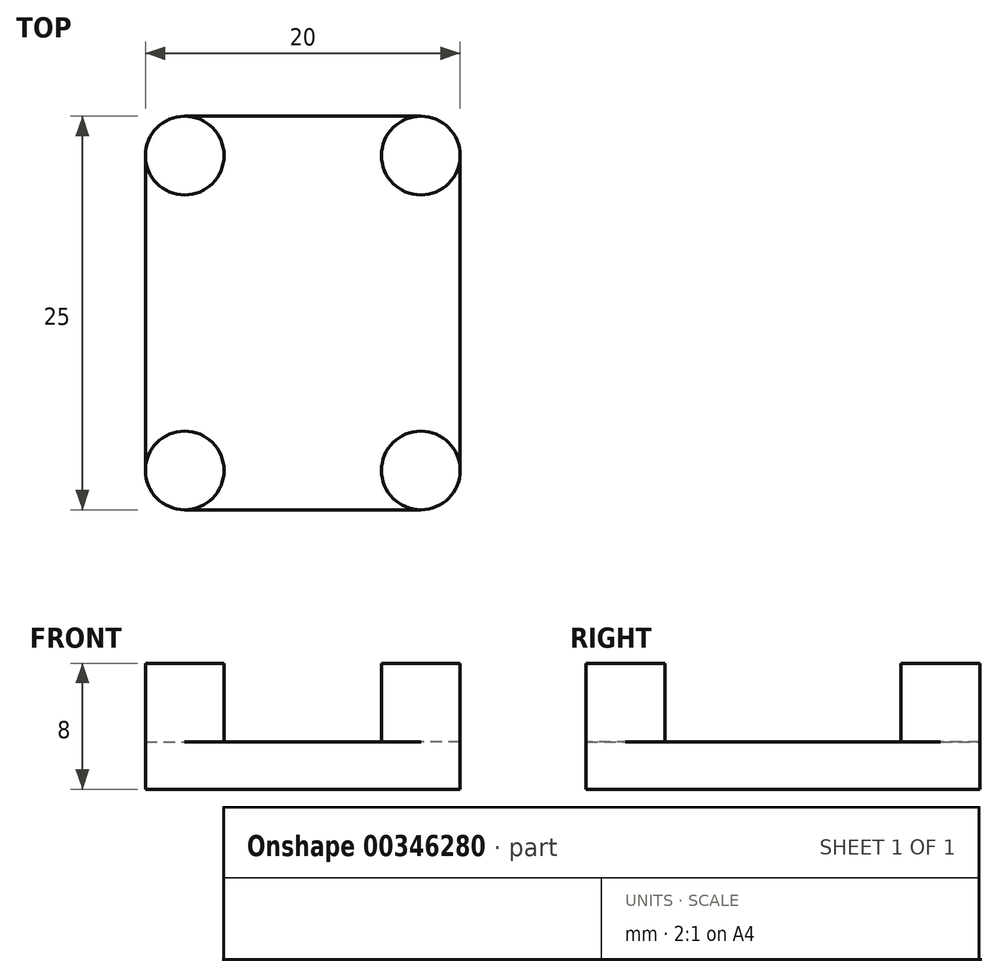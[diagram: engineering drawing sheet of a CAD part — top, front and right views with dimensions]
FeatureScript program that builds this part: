
annotation { "Feature Type Name" : "Feature", "Feature Type Description" : "" }
export const myFeature = defineFeature(function(context is Context, id is Id, definition is map)
    precondition{}
    {
        {
            var Q0;
            Q0=qCreatedBy(makeId("Top.planeOp"),FACE);
            var sketch = newSketch(context, id + "F0", { "sketchPlane" : qUnion([Q0])});
            skLineSegment(sketch, "E0.bottom", {"start": v(7.5, 10) * mm, "end": v(-7.5, 10) * mm, "construction": true});
            skLineSegment(sketch, "E0.top", {"start": v(7.5, -10) * mm, "end": v(-7.5, -10) * mm, "construction": true});
            skLineSegment(sketch, "E0.left", {"start": v(7.5, 10) * mm, "end": v(7.5, -10) * mm, "construction": true});
            skLineSegment(sketch, "E0.right", {"start": v(-7.5, 10) * mm, "end": v(-7.5, -10) * mm, "construction": true});
            skPoint(sketch, "E0.middle", {"position": v(0, 0) * mm});
            skCircle(sketch, "E1", {"center": v(-7.5, 10) * mm, "radius": 2.5 * mm});
            skCircle(sketch, "E2", {"center": v(7.5, 10) * mm, "radius": 2.5 * mm});
            skCircle(sketch, "E3", {"center": v(7.5, -10) * mm, "radius": 2.5 * mm});
            skCircle(sketch, "E4", {"center": v(-7.5, -10) * mm, "radius": 2.5 * mm});
            skLineSegment(sketch, "E5", {"start": v(-10, 10) * mm, "end": v(-10, -10) * mm});
            skLineSegment(sketch, "E6", {"start": v(-7.5, -12.5) * mm, "end": v(7.5, -12.5) * mm});
            skLineSegment(sketch, "E7", {"start": v(10, -10) * mm, "end": v(10, 10) * mm});
            skLineSegment(sketch, "E8", {"start": v(7.5, 12.5) * mm, "end": v(-7.5, 12.5) * mm});
            skSolve(sketch);
        }
        {
            var Q0;
            {var subQ0=sQuery(id+"F0.wireOp",EDGE,"E5");Q0=makeQuery(id+"F0.imprint","IMPRINT",FACE,{"disambiguationData":[TD([[makeQuery(id+"F0.imprint","IMPRINT",EDGE,{"derivedFrom":subQ0}),1.0]])]});}
            var Q1;
            {var subQ0=sQuery(id+"F0.wireOp",EDGE,"E3");var subQ1=makeQuery(id+"F0.imprint","INTERSECT",VERTEX,{"derivedFrom":[subQ0,sQuery(id+"F0.wireOp",EDGE,"E6")]});Q1=makeQuery(id+"F0.imprint","IMPRINT",FACE,{"disambiguationData":[TD([[makeQuery(id+"F0.imprint","IMPRINT",EDGE,{"disambiguationData":[TD([[subQ1,1.0]])],"derivedFrom":subQ0}),1.0]])]});}
            var Q2;
            {var subQ0=sQuery(id+"F0.wireOp",EDGE,"E4");var subQ1=makeQuery(id+"F0.imprint","INTERSECT",VERTEX,{"derivedFrom":[subQ0,sQuery(id+"F0.wireOp",EDGE,"E5")]});Q2=makeQuery(id+"F0.imprint","IMPRINT",FACE,{"disambiguationData":[TD([[makeQuery(id+"F0.imprint","IMPRINT",EDGE,{"disambiguationData":[TD([[subQ1,-1.0]])],"derivedFrom":subQ0}),1.0]])]});}
            var Q3;
            {var subQ0=sQuery(id+"F0.wireOp",EDGE,"E1");var subQ1=makeQuery(id+"F0.imprint","INTERSECT",VERTEX,{"derivedFrom":[subQ0,sQuery(id+"F0.wireOp",EDGE,"E5")]});Q3=makeQuery(id+"F0.imprint","IMPRINT",FACE,{"disambiguationData":[TD([[makeQuery(id+"F0.imprint","IMPRINT",EDGE,{"disambiguationData":[TD([[subQ1,1.0]])],"derivedFrom":subQ0}),1.0]])]});}
            var Q4;
            {var subQ0=sQuery(id+"F0.wireOp",EDGE,"E2");var subQ1=makeQuery(id+"F0.imprint","INTERSECT",VERTEX,{"derivedFrom":[subQ0,sQuery(id+"F0.wireOp",EDGE,"E7")]});Q4=makeQuery(id+"F0.imprint","IMPRINT",FACE,{"disambiguationData":[TD([[makeQuery(id+"F0.imprint","IMPRINT",EDGE,{"disambiguationData":[TD([[subQ1,-1.0]])],"derivedFrom":subQ0}),1.0]])]});}
            extrude(context, id + "F1", {"entities" : qUnion([Q0, Q1, Q2, Q3, Q4]), "oppositeDirection" : true, "depth" : 3 * mm});
        }
        {
            var Q0;
            {var subQ0=sQuery(id+"F0.wireOp",EDGE,"E4");var subQ1=makeQuery(id+"F0.imprint","INTERSECT",VERTEX,{"derivedFrom":[subQ0,sQuery(id+"F0.wireOp",EDGE,"E5")]});Q0=makeQuery(id+"F0.imprint","IMPRINT",FACE,{"disambiguationData":[TD([[makeQuery(id+"F0.imprint","IMPRINT",EDGE,{"disambiguationData":[TD([[subQ1,-1.0]])],"derivedFrom":subQ0}),1.0]])]});}
            var Q1;
            {var subQ0=sQuery(id+"F0.wireOp",EDGE,"E3");var subQ1=makeQuery(id+"F0.imprint","INTERSECT",VERTEX,{"derivedFrom":[subQ0,sQuery(id+"F0.wireOp",EDGE,"E6")]});Q1=makeQuery(id+"F0.imprint","IMPRINT",FACE,{"disambiguationData":[TD([[makeQuery(id+"F0.imprint","IMPRINT",EDGE,{"disambiguationData":[TD([[subQ1,1.0]])],"derivedFrom":subQ0}),1.0]])]});}
            var Q2;
            {var subQ0=sQuery(id+"F0.wireOp",EDGE,"E2");var subQ1=makeQuery(id+"F0.imprint","INTERSECT",VERTEX,{"derivedFrom":[subQ0,sQuery(id+"F0.wireOp",EDGE,"E7")]});Q2=makeQuery(id+"F0.imprint","IMPRINT",FACE,{"disambiguationData":[TD([[makeQuery(id+"F0.imprint","IMPRINT",EDGE,{"disambiguationData":[TD([[subQ1,-1.0]])],"derivedFrom":subQ0}),1.0]])]});}
            var Q3;
            {var subQ0=sQuery(id+"F0.wireOp",EDGE,"E1");var subQ1=makeQuery(id+"F0.imprint","INTERSECT",VERTEX,{"derivedFrom":[subQ0,sQuery(id+"F0.wireOp",EDGE,"E5")]});Q3=makeQuery(id+"F0.imprint","IMPRINT",FACE,{"disambiguationData":[TD([[makeQuery(id+"F0.imprint","IMPRINT",EDGE,{"disambiguationData":[TD([[subQ1,1.0]])],"derivedFrom":subQ0}),1.0]])]});}
            extrude(context, id + "F2", {"entities" : qUnion([Q0, Q1, Q2, Q3]), "operationType" : NewBodyOperationType.ADD, "depth" : 5 * mm});
        }
    });
